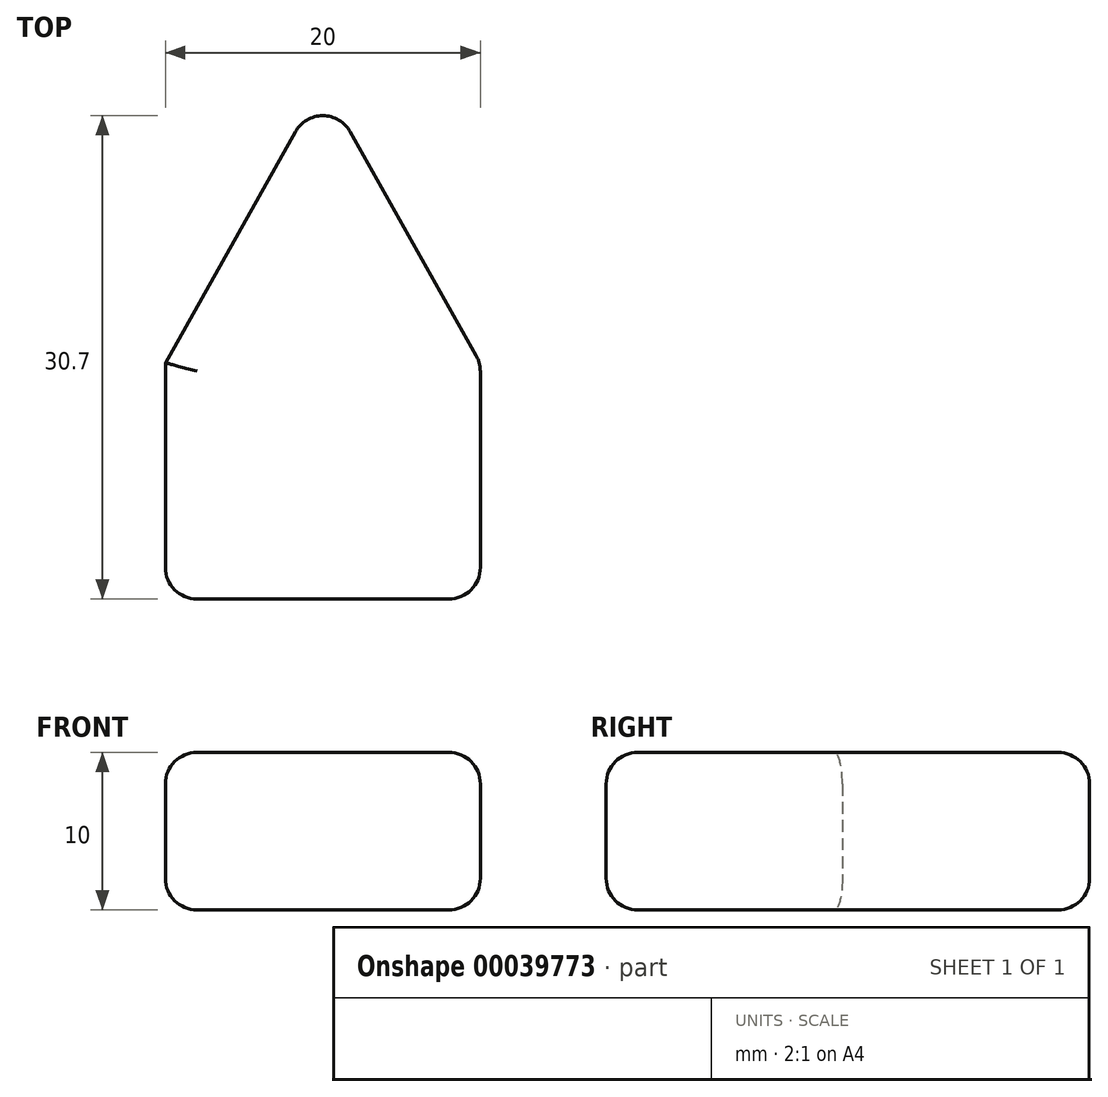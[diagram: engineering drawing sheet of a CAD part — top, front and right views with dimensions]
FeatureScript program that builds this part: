
annotation { "Feature Type Name" : "Feature", "Feature Type Description" : "" }
export const myFeature = defineFeature(function(context is Context, id is Id, definition is map)
    precondition{}
    {
        {
            var Q0;
            Q0=qCreatedBy(makeId("Top.planeOp"),FACE);
            var sketch = newSketch(context, id + "F0", { "sketchPlane" : qUnion([Q0])});
            skLineSegment(sketch, "E0.rect.bottom", {"start": v(-10, -8.21) * mm, "end": v(10, -8.21) * mm});
            skLineSegment(sketch, "E0.rect.top", {"start": v(-10, 6.79) * mm, "end": v(10, 6.79) * mm});
            skLineSegment(sketch, "E0.rect.left", {"start": v(-10, -8.21) * mm, "end": v(-10, 6.79) * mm});
            skLineSegment(sketch, "E0.rect.right", {"start": v(10, -8.21) * mm, "end": v(10, 6.79) * mm});
            skPoint(sketch, "E0.rect.middle", {"position": v(0, -0.71) * mm});
            skLineSegment(sketch, "E1", {"start": v(-10, 6.79) * mm, "end": v(0, 24.57) * mm});
            skLineSegment(sketch, "E2", {"start": v(0, 24.57) * mm, "end": v(10, 6.79) * mm});
            skSolve(sketch);
        }
        {
            var Q0;
            Q0=makeQuery(id+"F0.imprint","IMPRINT",FACE,{"disambiguationData":[TD([[makeQuery(id+"F0.imprint","IMPRINT",EDGE,{"derivedFrom":sQuery(id+"F0.wireOp",EDGE,"E0.rect.top")}),1.0]])]});
            var Q1;
            Q1=makeQuery(id+"F0.imprint","IMPRINT",FACE,{"disambiguationData":[TD([[makeQuery(id+"F0.imprint","IMPRINT",EDGE,{"derivedFrom":sQuery(id+"F0.wireOp",EDGE,"E0.rect.bottom")}),1.0]])]});
            extrude(context, id + "F1", {"entities" : qUnion([Q0, Q1]), "depth" : 10 * mm});
        }
        {
            var Q0;
            Q0=makeQuery(id+"F1.opExtrude","CAP_EDGE",EDGE,{"disambiguationData":[OSD([sQuery(id+"F0.wireOp",EDGE,"E2")])],"isStart":false});
            var Q1;
            Q1=makeQuery(id+"F1.opExtrude","CAP_EDGE",EDGE,{"disambiguationData":[OSD([sQuery(id+"F0.wireOp",EDGE,"E1")])],"isStart":false});
            var Q2;
            Q2=makeQuery(id+"F1.opExtrude","CAP_EDGE",EDGE,{"disambiguationData":[OSD([sQuery(id+"F0.wireOp",EDGE,"E0.rect.left")])],"isStart":false});
            var Q3;
            Q3=makeQuery(id+"F1.opExtrude","CAP_EDGE",EDGE,{"disambiguationData":[OSD([sQuery(id+"F0.wireOp",EDGE,"E0.rect.bottom")])],"isStart":false});
            var Q4;
            Q4=makeQuery(id+"F1.opExtrude","CAP_EDGE",EDGE,{"disambiguationData":[OSD([sQuery(id+"F0.wireOp",EDGE,"E0.rect.right")])],"isStart":false});
            var Q5;
            Q5=makeQuery(id+"F1.opExtrude","SWEPT_EDGE",EDGE,{"disambiguationData":[OSD([sQuery(id+"F0.wireOp",EDGE,"E0.rect.bottom"),sQuery(id+"F0.wireOp",EDGE,"E0.rect.right")])]});
            var Q6;
            Q6=makeQuery(id+"F1.opExtrude","CAP_EDGE",EDGE,{"disambiguationData":[OSD([sQuery(id+"F0.wireOp",EDGE,"E0.rect.right")])],"isStart":true});
            var Q7;
            Q7=makeQuery(id+"F1.opExtrude","SWEPT_EDGE",EDGE,{"disambiguationData":[OSD([sQuery(id+"F0.wireOp",EDGE,"E0.rect.top"),sQuery(id+"F0.wireOp",EDGE,"E0.rect.right"),sQuery(id+"F0.wireOp",EDGE,"E2")])]});
            var Q8;
            Q8=makeQuery(id+"F1.opExtrude","CAP_EDGE",EDGE,{"disambiguationData":[OSD([sQuery(id+"F0.wireOp",EDGE,"E2")])],"isStart":true});
            var Q9;
            Q9=makeQuery(id+"F1.opExtrude","SWEPT_EDGE",EDGE,{"disambiguationData":[OSD([sQuery(id+"F0.wireOp",EDGE,"E1"),sQuery(id+"F0.wireOp",EDGE,"E2")])]});
            var Q10;
            Q10=makeQuery(id+"F1.opExtrude","SWEPT_EDGE",EDGE,{"disambiguationData":[OSD([sQuery(id+"F0.wireOp",EDGE,"E0.rect.bottom"),sQuery(id+"F0.wireOp",EDGE,"E0.rect.left")])]});
            var Q11;
            Q11=makeQuery(id+"F1.opExtrude","CAP_EDGE",EDGE,{"disambiguationData":[OSD([sQuery(id+"F0.wireOp",EDGE,"E0.rect.bottom")])],"isStart":true});
            fillet(context, id + "F2", {"entities" : qUnion([Q0, Q1, Q2, Q3, Q4, Q5, Q6, Q7, Q8, Q9, Q10, Q11]), "radius" : 2 * mm, "tangentPropagation" : true, "allowEdgeOverflow" : false});
        }
        {
            var Q0;
            Q0=makeQuery(id+"F1.opExtrude","CAP_EDGE",EDGE,{"disambiguationData":[OSD([sQuery(id+"F0.wireOp",EDGE,"E0.rect.left")])],"isStart":true});
            var Q1;
            Q1=makeQuery(id+"F1.opExtrude","CAP_EDGE",EDGE,{"disambiguationData":[OSD([sQuery(id+"F0.wireOp",EDGE,"E1")])],"isStart":true});
            var Q2;
            {var subQ0=sQuery(id+"F0.wireOp",EDGE,"E2");Q2=makeQuery(id+"F2.opFillet","BLEND_EDGE",EDGE,{"blendedFrom":[makeQuery(id+"F1.opExtrude","CAP_EDGE",EDGE,{"disambiguationData":[OSD([subQ0])],"isStart":true}),makeQuery(id+"F1.opExtrude","CAP_FACE",FACE,{"disambiguationData":[OSD([sQuery(id+"F0.wireOp",EDGE,"E0.rect.bottom"),sQuery(id+"F0.wireOp",EDGE,"E0.rect.left"),sQuery(id+"F0.wireOp",EDGE,"E0.rect.right"),sQuery(id+"F0.wireOp",EDGE,"E1"),subQ0])],"isStart":true})],"blendedInto":[makeQuery(id+"F1.opExtrude","CAP_FACE",FACE,{"disambiguationData":[OSD([sQuery(id+"F0.wireOp",EDGE,"E0.rect.bottom"),sQuery(id+"F0.wireOp",EDGE,"E0.rect.left"),sQuery(id+"F0.wireOp",EDGE,"E0.rect.right"),sQuery(id+"F0.wireOp",EDGE,"E1"),subQ0])],"isStart":true})]});}
            var Q3;
            {var subQ0=sQuery(id+"F0.wireOp",EDGE,"E0.rect.right");Q3=makeQuery(id+"F2.opFillet","BLEND_EDGE",EDGE,{"blendedFrom":[makeQuery(id+"F1.opExtrude","CAP_EDGE",EDGE,{"disambiguationData":[OSD([subQ0])],"isStart":true}),makeQuery(id+"F1.opExtrude","CAP_FACE",FACE,{"disambiguationData":[OSD([sQuery(id+"F0.wireOp",EDGE,"E0.rect.bottom"),sQuery(id+"F0.wireOp",EDGE,"E0.rect.left"),subQ0,sQuery(id+"F0.wireOp",EDGE,"E1"),sQuery(id+"F0.wireOp",EDGE,"E2")])],"isStart":true})],"blendedInto":[makeQuery(id+"F1.opExtrude","CAP_FACE",FACE,{"disambiguationData":[OSD([sQuery(id+"F0.wireOp",EDGE,"E0.rect.bottom"),sQuery(id+"F0.wireOp",EDGE,"E0.rect.left"),subQ0,sQuery(id+"F0.wireOp",EDGE,"E1"),sQuery(id+"F0.wireOp",EDGE,"E2")])],"isStart":true})]});}
            var Q4;
            {var subQ0=sQuery(id+"F0.wireOp",EDGE,"E0.rect.bottom");Q4=makeQuery(id+"F2.opFillet","BLEND_EDGE",EDGE,{"blendedFrom":[makeQuery(id+"F1.opExtrude","CAP_EDGE",EDGE,{"disambiguationData":[OSD([subQ0])],"isStart":true}),makeQuery(id+"F1.opExtrude","SWEPT_FACE",FACE,{"disambiguationData":[OSD([subQ0])]})],"blendedInto":[makeQuery(id+"F1.opExtrude","SWEPT_FACE",FACE,{"disambiguationData":[OSD([subQ0])]})]});}
            fillet(context, id + "F3", {"entities" : qUnion([Q0, Q1, Q2, Q3, Q4]), "radius" : 2 * mm, "tangentPropagation" : true, "allowEdgeOverflow" : false});
        }
    });
